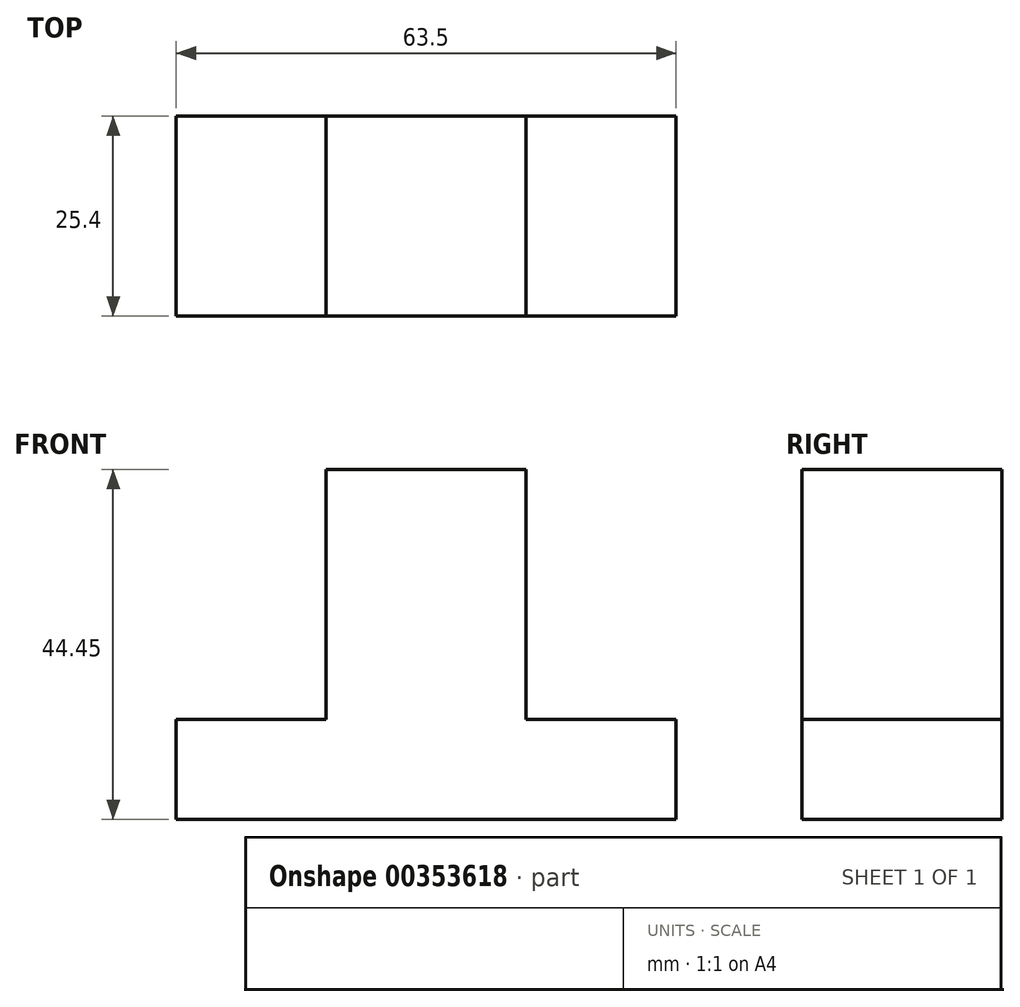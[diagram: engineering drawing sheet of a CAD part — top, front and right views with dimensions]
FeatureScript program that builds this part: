
annotation { "Feature Type Name" : "Feature", "Feature Type Description" : "" }
export const myFeature = defineFeature(function(context is Context, id is Id, definition is map)
    precondition{}
    {
        {
            var Q0;
            Q0=qCreatedBy(makeId("Front.planeOp"),FACE);
            var sketch = newSketch(context, id + "F0", { "sketchPlane" : qUnion([Q0])});
            skLineSegment(sketch, "E0", {"start": v(0, 0) * mm, "end": v(0, 12.7) * mm});
            skLineSegment(sketch, "E1", {"start": v(0, 12.7) * mm, "end": v(19.05, 12.7) * mm});
            skLineSegment(sketch, "E2", {"start": v(19.05, 12.7) * mm, "end": v(19.05, 44.45) * mm});
            skLineSegment(sketch, "E3", {"start": v(19.05, 44.45) * mm, "end": v(44.45, 44.45) * mm});
            skLineSegment(sketch, "E4", {"start": v(44.45, 44.45) * mm, "end": v(44.45, 12.7) * mm});
            skLineSegment(sketch, "E5", {"start": v(44.45, 12.7) * mm, "end": v(63.5, 12.7) * mm});
            skLineSegment(sketch, "E6", {"start": v(63.5, 12.7) * mm, "end": v(63.5, 0) * mm});
            skLineSegment(sketch, "E7", {"start": v(63.5, 0) * mm, "end": v(0, 0) * mm});
            skSolve(sketch);
        }
        {
            var Q0;
            Q0=makeQuery(id+"F0.imprint","IMPRINT",FACE,{"disambiguationData":[TD([[makeQuery(id+"F0.imprint","IMPRINT",EDGE,{"derivedFrom":sQuery(id+"F0.wireOp",EDGE,"E0")}),-1.0]])]});
            extrude(context, id + "F1", {"entities" : qUnion([Q0]), "depth" : 25.4 * mm});
        }
    });
